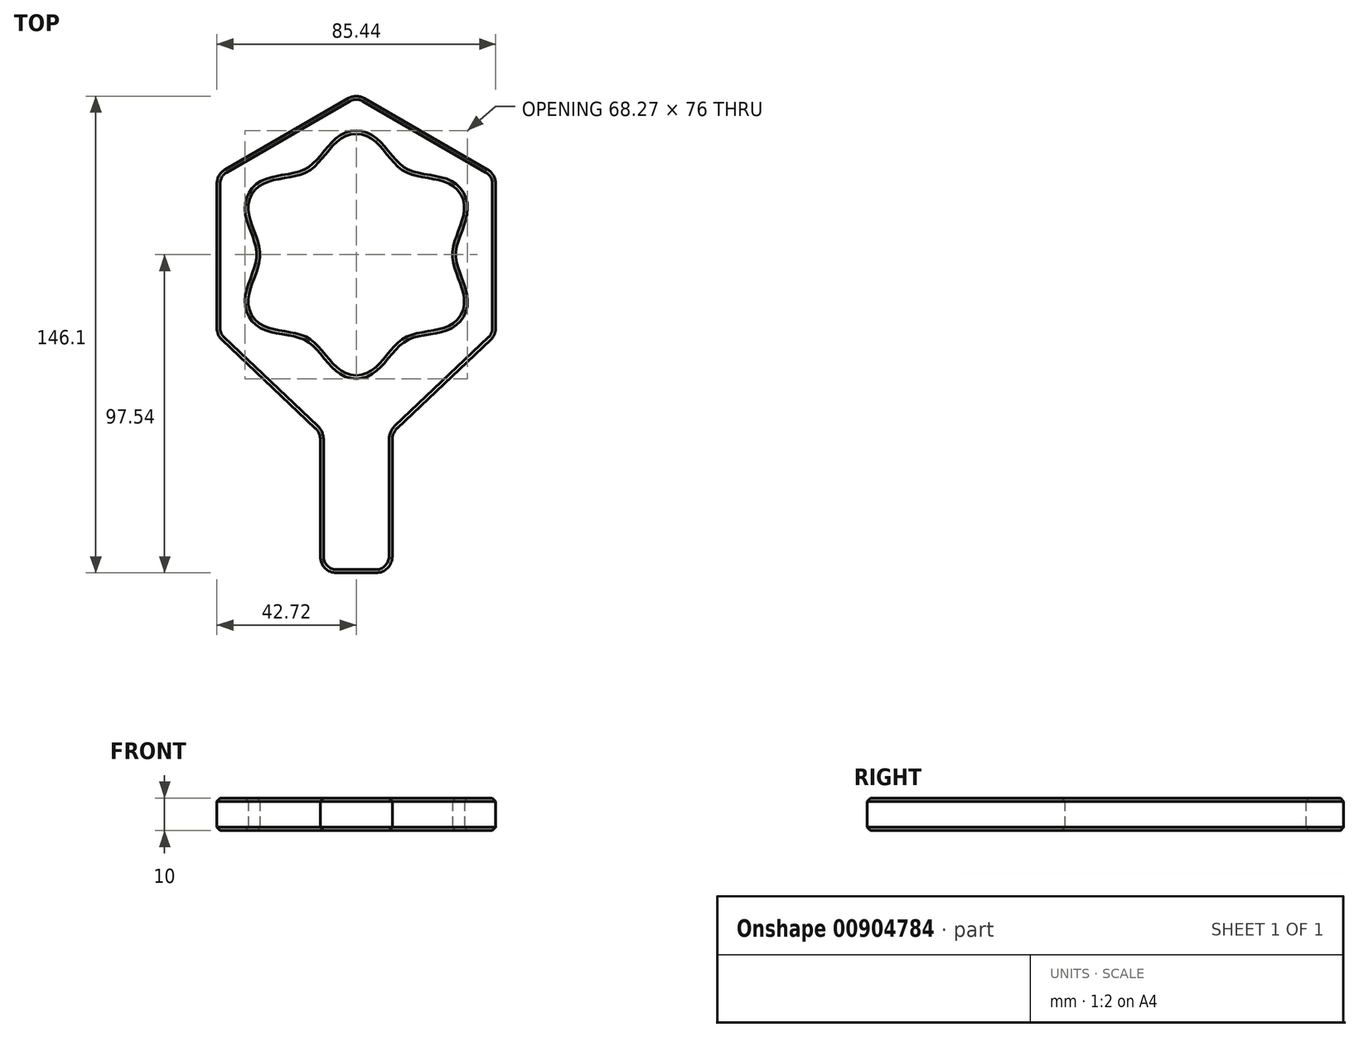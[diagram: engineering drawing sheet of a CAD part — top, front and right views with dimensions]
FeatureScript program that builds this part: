
annotation { "Feature Type Name" : "Feature", "Feature Type Description" : "" }
export const myFeature = defineFeature(function(context is Context, id is Id, definition is map)
    precondition{}
    {
        {
            var Q0;
            Q0=qCreatedBy(makeId("Top.planeOp"),FACE);
            var sketch = newSketch(context, id + "F0", { "sketchPlane" : qUnion([Q0])});
            skCircle(sketch, "E0.cCircle", {"center": v(0, 0) * mm, "radius": 32.04 * mm, "construction": true});
            skLineSegment(sketch, "E0.0", {"start": v(32.04, -18.5) * mm, "end": v(0, -37) * mm, "construction": true});
            skLineSegment(sketch, "E0.1", {"start": v(-32.04, -18.5) * mm, "end": v(0, -37) * mm, "construction": true});
            skLineSegment(sketch, "E0.2", {"start": v(-32.04, -18.5) * mm, "end": v(-32.04, 18.5) * mm, "construction": true});
            skLineSegment(sketch, "E0.3", {"start": v(-32.04, 18.5) * mm, "end": v(0, 37) * mm, "construction": true});
            skLineSegment(sketch, "E0.4", {"start": v(32.04, 18.5) * mm, "end": v(0, 37) * mm, "construction": true});
            skLineSegment(sketch, "E0.5", {"start": v(32.04, 18.5) * mm, "end": v(32.04, -18.5) * mm, "construction": true});
            skPoint(sketch, "E0.0.midPoint", {"position": v(16.02, -27.75) * mm});
            skLineSegment(sketch, "E1", {"start": v(0, 37) * mm, "end": v(21.36, 37) * mm, "construction": true});
            skCircle(sketch, "E2.cCircle", {"center": v(0, 0) * mm, "radius": 25.55 * mm, "construction": true});
            skLineSegment(sketch, "E2.0", {"start": v(14.75, 25.55) * mm, "end": v(29.5, 0) * mm, "construction": true});
            skLineSegment(sketch, "E2.1", {"start": v(29.5, 0) * mm, "end": v(14.75, -25.55) * mm, "construction": true});
            skLineSegment(sketch, "E2.2", {"start": v(14.75, -25.55) * mm, "end": v(-14.75, -25.55) * mm, "construction": true});
            skLineSegment(sketch, "E2.3", {"start": v(-14.75, -25.55) * mm, "end": v(-29.5, 0) * mm, "construction": true});
            skLineSegment(sketch, "E2.4", {"start": v(-29.5, 0) * mm, "end": v(-14.75, 25.55) * mm, "construction": true});
            skLineSegment(sketch, "E2.5", {"start": v(-14.75, 25.55) * mm, "end": v(14.75, 25.55) * mm, "construction": true});
            skPoint(sketch, "E2.0.midPoint", {"position": v(22.13, 12.77) * mm});
            skFitSpline(sketch, "E3", {"points": [v(32.04, 18.5) * mm, v(14.75, 25.55) * mm, v(0, 37) * mm], "startDerivative": vector(-21, 36.37) * mm, "endDerivative": vector(-42, 0) * mm});
            skLineSegment(sketch, "E4", {"start": v(32.04, 18.5) * mm, "end": v(21.36, 37) * mm, "construction": true});
            skLineSegment(sketch, "E5", {"start": v(0, 37) * mm, "end": v(0, 49.33) * mm});
            skLineSegment(sketch, "E6", {"start": v(0, 49.33) * mm, "end": v(42.72, 24.67) * mm});
            skLineSegment(sketch, "E7", {"start": v(42.72, 24.67) * mm, "end": v(32.04, 18.5) * mm});
            skSolve(sketch);
        }
        {
            var Q0;
            Q0 = qSketchRegion(id + "F0", true);
            extrude(context, id + "F1", {"entities" : qUnion([Q0]), "depth" : 10 * mm, "offsetDistance" : 25 * mm});
        }
        {
            var Q0;
            Q0=qCreatedBy(makeId("Right.planeOp"),FACE);
            var sketch = newSketch(context, id + "F2", { "sketchPlane" : qUnion([Q0])});
            skLineSegment(sketch, "E8", {"start": v(0, -17.17) * mm, "end": v(0, 19.24) * mm});
            skSolve(sketch);
        }
        {
            var Q0;
            Q0=makeQuery(id+"F1.opExtrude","SWEPT_BODY",BODY,{"disambiguationData":[OSD([sQuery(id+"F0.wireOp",EDGE,"E3"),sQuery(id+"F0.wireOp",EDGE,"E5"),sQuery(id+"F0.wireOp",EDGE,"E6"),sQuery(id+"F0.wireOp",EDGE,"E7")])]});
            var Q1;
            Q1=sQuery(id+"F2.wireOp",EDGE,"E8");
            circularPattern(context, id + "F3", {"entities" : qUnion([Q0]), "axis" : qUnion([Q1]), "angle" : 360 * degree, "instanceCount" : 6, "equalSpace" : true});
        }
        {
            var Q0;
            Q0=makeQuery(id+"F1.opExtrude","SWEPT_BODY",BODY,{"disambiguationData":[OSD([sQuery(id+"F0.wireOp",EDGE,"E3"),sQuery(id+"F0.wireOp",EDGE,"E5"),sQuery(id+"F0.wireOp",EDGE,"E6"),sQuery(id+"F0.wireOp",EDGE,"E7")])]});
            var Q1;
            Q1=makeQuery(id+"F3.opPattern","COPY",BODY,{"derivedFrom":makeQuery(id+"F1.opExtrude","SWEPT_BODY",BODY,{"disambiguationData":[OSD([sQuery(id+"F0.wireOp",EDGE,"E3"),sQuery(id+"F0.wireOp",EDGE,"E5"),sQuery(id+"F0.wireOp",EDGE,"E6"),sQuery(id+"F0.wireOp",EDGE,"E7")])]}),"instanceName":"1"});
            var Q2;
            Q2=makeQuery(id+"F3.opPattern","COPY",BODY,{"derivedFrom":makeQuery(id+"F1.opExtrude","SWEPT_BODY",BODY,{"disambiguationData":[OSD([sQuery(id+"F0.wireOp",EDGE,"E3"),sQuery(id+"F0.wireOp",EDGE,"E5"),sQuery(id+"F0.wireOp",EDGE,"E6"),sQuery(id+"F0.wireOp",EDGE,"E7")])]}),"instanceName":"2"});
            var Q3;
            Q3=makeQuery(id+"F3.opPattern","COPY",BODY,{"derivedFrom":makeQuery(id+"F1.opExtrude","SWEPT_BODY",BODY,{"disambiguationData":[OSD([sQuery(id+"F0.wireOp",EDGE,"E3"),sQuery(id+"F0.wireOp",EDGE,"E5"),sQuery(id+"F0.wireOp",EDGE,"E6"),sQuery(id+"F0.wireOp",EDGE,"E7")])]}),"instanceName":"3"});
            var Q4;
            Q4=makeQuery(id+"F3.opPattern","COPY",BODY,{"derivedFrom":makeQuery(id+"F1.opExtrude","SWEPT_BODY",BODY,{"disambiguationData":[OSD([sQuery(id+"F0.wireOp",EDGE,"E3"),sQuery(id+"F0.wireOp",EDGE,"E5"),sQuery(id+"F0.wireOp",EDGE,"E6"),sQuery(id+"F0.wireOp",EDGE,"E7")])]}),"instanceName":"4"});
            var Q5;
            Q5=makeQuery(id+"F3.opPattern","COPY",BODY,{"derivedFrom":makeQuery(id+"F1.opExtrude","SWEPT_BODY",BODY,{"disambiguationData":[OSD([sQuery(id+"F0.wireOp",EDGE,"E3"),sQuery(id+"F0.wireOp",EDGE,"E5"),sQuery(id+"F0.wireOp",EDGE,"E6"),sQuery(id+"F0.wireOp",EDGE,"E7")])]}),"instanceName":"5"});
            booleanBodies(context, id + "F4", {"operationType" : BooleanOperationType.UNION, "tools" : qUnion([Q0, Q1, Q2, Q3, Q4, Q5])});
        }
        {
            var Q0;
            Q0=qCreatedBy(makeId("Top.planeOp"),FACE);
            var sketch = newSketch(context, id + "F5", { "sketchPlane" : qUnion([Q0])});
            skPoint(sketch, "E9.0", {"position": v(-42.72, -24.67) * mm});
            skPoint(sketch, "E10.0", {"position": v(42.72, -24.67) * mm});
            skPoint(sketch, "E11.0", {"position": v(0, -49.33) * mm});
            skLineSegment(sketch, "E12.0", {"start": v(0, -49.33) * mm, "end": v(-42.72, -24.67) * mm, "construction": true});
            skLineSegment(sketch, "E13.0", {"start": v(42.72, -24.67) * mm, "end": v(0, -49.33) * mm, "construction": true});
            skLineSegment(sketch, "E14", {"start": v(-42.72, -24.67) * mm, "end": v(-11.03, -54.6) * mm});
            skLineSegment(sketch, "E15", {"start": v(-11.03, -54.6) * mm, "end": v(-11.03, -97.54) * mm});
            skLineSegment(sketch, "E16", {"start": v(-11.03, -97.54) * mm, "end": v(0, -97.54) * mm});
            skLineSegment(sketch, "E17", {"start": v(-42.72, -24.67) * mm, "end": v(0, -49.33) * mm});
            skLineSegment(sketch, "E18.MirrorCS", {"start": v(42.72, -24.67) * mm, "end": v(0, -49.33) * mm});
            skLineSegment(sketch, "E19.MirrorCS", {"start": v(11.03, -97.54) * mm, "end": v(0, -97.54) * mm});
            skLineSegment(sketch, "E20.MirrorCS", {"start": v(42.72, -24.67) * mm, "end": v(11.03, -54.6) * mm});
            skLineSegment(sketch, "E21.MirrorCS", {"start": v(11.03, -54.6) * mm, "end": v(11.03, -97.54) * mm});
            skSolve(sketch);
        }
        {
            var Q0;
            Q0 = qSketchRegion(id + "F5", true);
            var Q1;
            {var subQ0=makeQuery(id+"F1.opExtrude","CAP_FACE",FACE,{"disambiguationData":[OSD([sQuery(id+"F0.wireOp",EDGE,"E3"),sQuery(id+"F0.wireOp",EDGE,"E5"),sQuery(id+"F0.wireOp",EDGE,"E6"),sQuery(id+"F0.wireOp",EDGE,"E7")])],"isStart":false});Q1=makeQuery(id+"F4.opBoolean","MERGE",FACE,{"derivedFrom":[subQ0,makeQuery(id+"F3.opPattern","COPY",FACE,{"derivedFrom":subQ0,"instanceName":"1"}),makeQuery(id+"F3.opPattern","COPY",FACE,{"derivedFrom":subQ0,"instanceName":"2"}),makeQuery(id+"F3.opPattern","COPY",FACE,{"derivedFrom":subQ0,"instanceName":"3"}),makeQuery(id+"F3.opPattern","COPY",FACE,{"derivedFrom":subQ0,"instanceName":"4"}),makeQuery(id+"F3.opPattern","COPY",FACE,{"derivedFrom":subQ0,"instanceName":"5"})]});}
            extrude(context, id + "F6", {"entities" : qUnion([Q0]), "operationType" : NewBodyOperationType.ADD, "endBound" : BoundingType.UP_TO_SURFACE, "depth" : 25 * mm, "endBoundEntityFace" : qUnion([Q1]), "offsetDistance" : 25 * mm});
        }
        {
            var Q0;
            {var subQ0=sQuery(id+"F0.wireOp",EDGE,"E6");Q0=makeQuery(id+"F4.opBoolean","MERGE",EDGE,{"derivedFrom":[makeQuery(id+"F1.opExtrude","SWEPT_EDGE",EDGE,{"disambiguationData":[OSD([sQuery(id+"F0.wireOp",EDGE,"E5"),subQ0])]}),makeQuery(id+"F3.opPattern","COPY",EDGE,{"derivedFrom":makeQuery(id+"F1.opExtrude","SWEPT_EDGE",EDGE,{"disambiguationData":[OSD([subQ0,sQuery(id+"F0.wireOp",EDGE,"E7")])]}),"instanceName":"1"})]});}
            var Q1;
            {var subQ0=sQuery(id+"F0.wireOp",EDGE,"E6");Q1=makeQuery(id+"F4.opBoolean","MERGE",EDGE,{"derivedFrom":[makeQuery(id+"F1.opExtrude","SWEPT_EDGE",EDGE,{"disambiguationData":[OSD([subQ0,sQuery(id+"F0.wireOp",EDGE,"E7")])]}),makeQuery(id+"F3.opPattern","COPY",EDGE,{"derivedFrom":makeQuery(id+"F1.opExtrude","SWEPT_EDGE",EDGE,{"disambiguationData":[OSD([sQuery(id+"F0.wireOp",EDGE,"E5"),subQ0])]}),"instanceName":"5"})]});}
            var Q2;
            {var subQ0=sQuery(id+"F0.wireOp",EDGE,"E6");Q2=makeQuery(id+"F4.opBoolean","MERGE",EDGE,{"derivedFrom":[makeQuery(id+"F3.opPattern","COPY",EDGE,{"derivedFrom":makeQuery(id+"F1.opExtrude","SWEPT_EDGE",EDGE,{"disambiguationData":[OSD([sQuery(id+"F0.wireOp",EDGE,"E5"),subQ0])]}),"instanceName":"4"}),makeQuery(id+"F3.opPattern","COPY",EDGE,{"derivedFrom":makeQuery(id+"F1.opExtrude","SWEPT_EDGE",EDGE,{"disambiguationData":[OSD([subQ0,sQuery(id+"F0.wireOp",EDGE,"E7")])]}),"instanceName":"5"})]});}
            var Q3;
            Q3=makeQuery(id+"F6.opExtrude","SWEPT_EDGE",EDGE,{"disambiguationData":[OSD([sQuery(id+"F5.wireOp",EDGE,"E18.MirrorCS"),sQuery(id+"F5.wireOp",EDGE,"E20.MirrorCS")])]});
            var Q4;
            Q4=makeQuery(id+"F6.opExtrude","SWEPT_EDGE",EDGE,{"disambiguationData":[OSD([sQuery(id+"F5.wireOp",EDGE,"E20.MirrorCS"),sQuery(id+"F5.wireOp",EDGE,"E21.MirrorCS")])]});
            var Q5;
            Q5=makeQuery(id+"F6.opExtrude","SWEPT_EDGE",EDGE,{"disambiguationData":[OSD([sQuery(id+"F5.wireOp",EDGE,"E19.MirrorCS"),sQuery(id+"F5.wireOp",EDGE,"E21.MirrorCS")])]});
            var Q6;
            Q6=makeQuery(id+"F6.opExtrude","SWEPT_EDGE",EDGE,{"disambiguationData":[OSD([sQuery(id+"F5.wireOp",EDGE,"E15"),sQuery(id+"F5.wireOp",EDGE,"E16")])]});
            var Q7;
            Q7=makeQuery(id+"F6.opExtrude","SWEPT_EDGE",EDGE,{"disambiguationData":[OSD([sQuery(id+"F5.wireOp",EDGE,"E14"),sQuery(id+"F5.wireOp",EDGE,"E15")])]});
            var Q8;
            Q8=makeQuery(id+"F6.opExtrude","SWEPT_EDGE",EDGE,{"disambiguationData":[OSD([sQuery(id+"F5.wireOp",EDGE,"E14"),sQuery(id+"F5.wireOp",EDGE,"E17")])]});
            var Q9;
            {var subQ0=sQuery(id+"F0.wireOp",EDGE,"E6");Q9=makeQuery(id+"F4.opBoolean","MERGE",EDGE,{"derivedFrom":[makeQuery(id+"F3.opPattern","COPY",EDGE,{"derivedFrom":makeQuery(id+"F1.opExtrude","SWEPT_EDGE",EDGE,{"disambiguationData":[OSD([sQuery(id+"F0.wireOp",EDGE,"E5"),subQ0])]}),"instanceName":"2"}),makeQuery(id+"F3.opPattern","COPY",EDGE,{"derivedFrom":makeQuery(id+"F1.opExtrude","SWEPT_EDGE",EDGE,{"disambiguationData":[OSD([subQ0,sQuery(id+"F0.wireOp",EDGE,"E7")])]}),"instanceName":"3"})]});}
            var Q10;
            {var subQ0=sQuery(id+"F0.wireOp",EDGE,"E6");Q10=makeQuery(id+"F4.opBoolean","MERGE",EDGE,{"derivedFrom":[makeQuery(id+"F3.opPattern","COPY",EDGE,{"derivedFrom":makeQuery(id+"F1.opExtrude","SWEPT_EDGE",EDGE,{"disambiguationData":[OSD([sQuery(id+"F0.wireOp",EDGE,"E5"),subQ0])]}),"instanceName":"1"}),makeQuery(id+"F3.opPattern","COPY",EDGE,{"derivedFrom":makeQuery(id+"F1.opExtrude","SWEPT_EDGE",EDGE,{"disambiguationData":[OSD([subQ0,sQuery(id+"F0.wireOp",EDGE,"E7")])]}),"instanceName":"2"})]});}
            fillet(context, id + "F7", {"entities" : qUnion([Q0, Q1, Q2, Q3, Q4, Q5, Q6, Q7, Q8, Q9, Q10]), "radius" : 5 * mm, "tangentPropagation" : true, "allowEdgeOverflow" : false});
        }
        {
            var Q0;
            {var subQ0=makeQuery(id+"F1.opExtrude","CAP_FACE",FACE,{"disambiguationData":[OSD([sQuery(id+"F0.wireOp",EDGE,"E3"),sQuery(id+"F0.wireOp",EDGE,"E5"),sQuery(id+"F0.wireOp",EDGE,"E6"),sQuery(id+"F0.wireOp",EDGE,"E7")])],"isStart":true});Q0=makeQuery(id+"F6.boolean.opBoolean","MERGE",FACE,{"derivedFrom":[makeQuery(id+"F4.opBoolean","MERGE",FACE,{"derivedFrom":[subQ0,makeQuery(id+"F3.opPattern","COPY",FACE,{"derivedFrom":subQ0,"instanceName":"1"}),makeQuery(id+"F3.opPattern","COPY",FACE,{"derivedFrom":subQ0,"instanceName":"2"}),makeQuery(id+"F3.opPattern","COPY",FACE,{"derivedFrom":subQ0,"instanceName":"3"}),makeQuery(id+"F3.opPattern","COPY",FACE,{"derivedFrom":subQ0,"instanceName":"4"}),makeQuery(id+"F3.opPattern","COPY",FACE,{"derivedFrom":subQ0,"instanceName":"5"})]}),makeQuery(id+"F6.opExtrude","CAP_FACE",FACE,{"disambiguationData":[OSD([sQuery(id+"F5.wireOp",EDGE,"E14"),sQuery(id+"F5.wireOp",EDGE,"E15"),sQuery(id+"F5.wireOp",EDGE,"E16"),sQuery(id+"F5.wireOp",EDGE,"E17"),sQuery(id+"F5.wireOp",EDGE,"E18.MirrorCS"),sQuery(id+"F5.wireOp",EDGE,"E19.MirrorCS"),sQuery(id+"F5.wireOp",EDGE,"E20.MirrorCS"),sQuery(id+"F5.wireOp",EDGE,"E21.MirrorCS")])],"isStart":true})]});}
            var Q1;
            {var subQ0=makeQuery(id+"F1.opExtrude","CAP_FACE",FACE,{"disambiguationData":[OSD([sQuery(id+"F0.wireOp",EDGE,"E3"),sQuery(id+"F0.wireOp",EDGE,"E5"),sQuery(id+"F0.wireOp",EDGE,"E6"),sQuery(id+"F0.wireOp",EDGE,"E7")])],"isStart":false});Q1=makeQuery(id+"F6.boolean.opBoolean","MERGE",FACE,{"derivedFrom":[makeQuery(id+"F4.opBoolean","MERGE",FACE,{"derivedFrom":[subQ0,makeQuery(id+"F3.opPattern","COPY",FACE,{"derivedFrom":subQ0,"instanceName":"1"}),makeQuery(id+"F3.opPattern","COPY",FACE,{"derivedFrom":subQ0,"instanceName":"2"}),makeQuery(id+"F3.opPattern","COPY",FACE,{"derivedFrom":subQ0,"instanceName":"3"}),makeQuery(id+"F3.opPattern","COPY",FACE,{"derivedFrom":subQ0,"instanceName":"4"}),makeQuery(id+"F3.opPattern","COPY",FACE,{"derivedFrom":subQ0,"instanceName":"5"})]}),makeQuery(id+"F6.opExtrude","CAP_FACE",FACE,{"disambiguationData":[OSD([sQuery(id+"F5.wireOp",EDGE,"E14"),sQuery(id+"F5.wireOp",EDGE,"E15"),sQuery(id+"F5.wireOp",EDGE,"E16"),sQuery(id+"F5.wireOp",EDGE,"E17"),sQuery(id+"F5.wireOp",EDGE,"E18.MirrorCS"),sQuery(id+"F5.wireOp",EDGE,"E19.MirrorCS"),sQuery(id+"F5.wireOp",EDGE,"E20.MirrorCS"),sQuery(id+"F5.wireOp",EDGE,"E21.MirrorCS")])],"isStart":false})]});}
            chamfer(context, id + "F8", {"entities" : qUnion([Q0, Q1]), "width" : 1 * mm, "tangentPropagation" : true});
        }
    });
